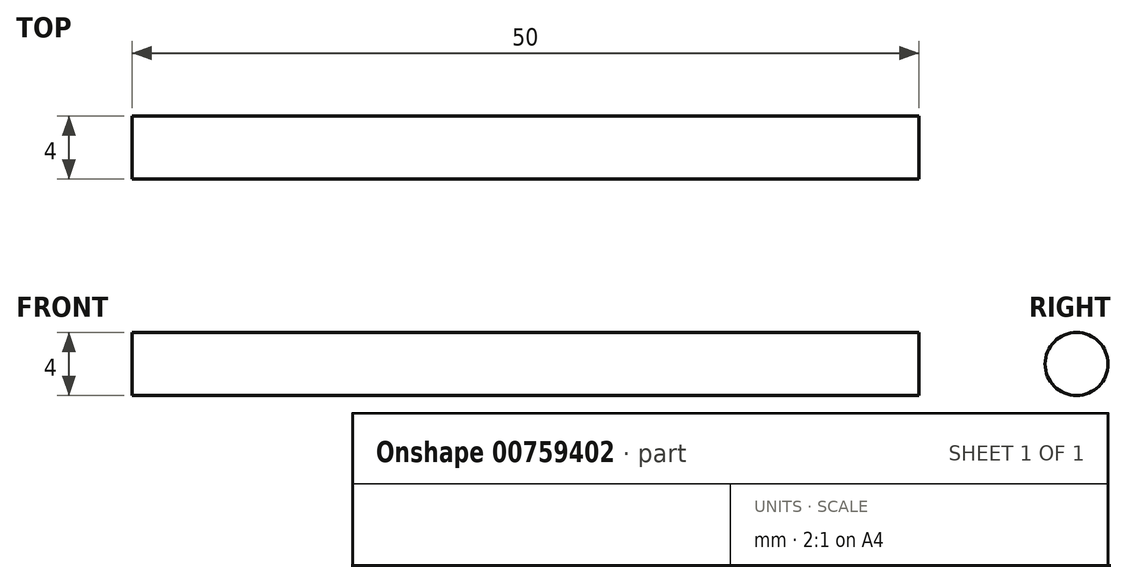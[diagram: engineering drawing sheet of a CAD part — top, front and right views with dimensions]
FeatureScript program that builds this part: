
annotation { "Feature Type Name" : "Feature", "Feature Type Description" : "" }
export const myFeature = defineFeature(function(context is Context, id is Id, definition is map)
    precondition{}
    {
        {
            var Q0;
            Q0=qCreatedBy(makeId("Right.planeOp"),FACE);
            var sketch = newSketch(context, id + "F0", { "sketchPlane" : qUnion([Q0])});
            skCircle(sketch, "E0", {"center": v(0, 0) * mm, "radius": 2 * mm});
            skSolve(sketch);
        }
        {
            var Q0;
            Q0 = qSketchRegion(id + "F0", true);
            extrude(context, id + "F1", {"entities" : qUnion([Q0]), "endBound" : BoundingType.SYMMETRIC, "depth" : 50 * mm, "offsetDistance" : 25 * mm});
        }
    });
